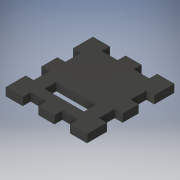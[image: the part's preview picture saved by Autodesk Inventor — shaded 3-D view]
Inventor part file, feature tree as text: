
AUTODESK INVENTOR PART (.ipt)
format: ipt  version: 2019 (Build 230136000, 136)  size: 167,936 bytes
history: native  units: mm
features: extrude x2, sketch x2
ambient origin geometry x8: Origin, YZ Plane, XZ Plane, XY Plane, X Axis, Y Axis, Z Axis, Center Point
bodies: Solid1 (feature_tree)
feature tree (4):
  extrude  "Extrusion1"  Depth=44.0mm
  extrude  "Extrusion2"  Depth=6.0mm
  sketch  "Sketch1"  dims[d0=41.0mm d1=44.0mm]
  sketch  "Sketch2"  dims[d2=20.0mm d3=6.0mm d4=10.5mm d5=9.0mm d6=4.0mm d7=0.0mm d8=4.0mm d9=8.0mm d10=4.0mm d11=8.0mm d12=4.0mm d13=4.0mm d14=0.0mm]
